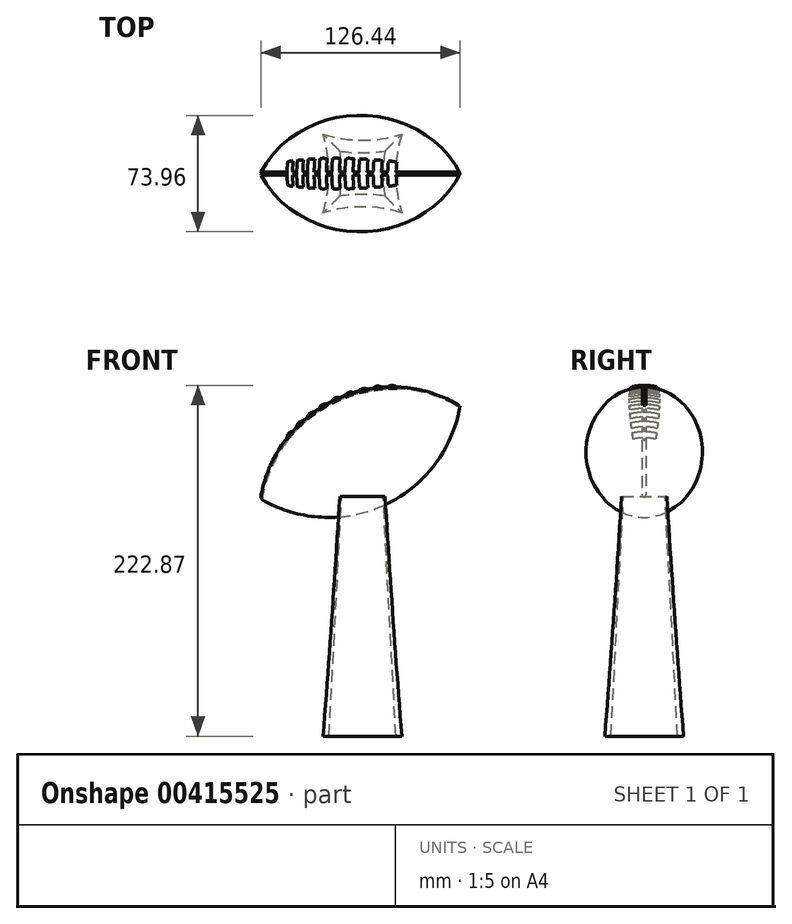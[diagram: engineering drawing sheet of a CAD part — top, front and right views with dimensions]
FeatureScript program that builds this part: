
annotation { "Feature Type Name" : "Feature", "Feature Type Description" : "" }
export const myFeature = defineFeature(function(context is Context, id is Id, definition is map)
    precondition{}
    {
        {
            var Q0;
            Q0=qCreatedBy(makeId("Top.planeOp"),FACE);
            var sketch = newSketch(context, id + "F0", { "sketchPlane" : qUnion([Q0])});
            skLineSegment(sketch, "E0.bottom", {"start": v(25, -25) * mm, "end": v(-25, -25) * mm, "construction": true});
            skLineSegment(sketch, "E0.top", {"start": v(25, 25) * mm, "end": v(-25, 25) * mm, "construction": true});
            skLineSegment(sketch, "E0.left", {"start": v(25, -25) * mm, "end": v(25, 25) * mm, "construction": true});
            skLineSegment(sketch, "E0.right", {"start": v(-25, -25) * mm, "end": v(-25, 25) * mm, "construction": true});
            skPoint(sketch, "E0.middle", {"position": v(0, 0) * mm});
            skArc(sketch, "E1", {"start": v(-25, -25) * mm, "mid": v(-21.18, 0) * mm, "end": v(-25, 25) * mm});
            skArc(sketch, "E2.1.0", {"start": v(25, -25) * mm, "mid": v(0, -21.18) * mm, "end": v(-25, -25) * mm});
            skArc(sketch, "E2.2.0", {"start": v(25, 25) * mm, "mid": v(21.18, 0) * mm, "end": v(25, -25) * mm});
            skArc(sketch, "E2.3.0", {"start": v(-25, 25) * mm, "mid": v(0, 21.18) * mm, "end": v(25, 25) * mm});
            skSolve(sketch);
        }
        {
            var Q0;
            Q0=makeQuery(id+"F0.imprint","IMPRINT",FACE,{"disambiguationData":[TD([[makeQuery(id+"F0.imprint","IMPRINT",EDGE,{"derivedFrom":sQuery(id+"F0.wireOp",EDGE,"E1")}),-1.0]])]});
            extrude(context, id + "F1", {"entities" : qUnion([Q0]), "depth" : 152.4 * mm, "hasDraft" : true, "draftAngle" : 3 * degree, "draftPullDirection" : true});
        }
        {
            var Q0;
            Q0=qCreatedBy(makeId("Front.planeOp"),FACE);
            var sketch = newSketch(context, id + "F2", { "sketchPlane" : qUnion([Q0])});
            skLineSegment(sketch, "E3", {"start": v(91.8, 223.9) * mm, "end": v(-91.96, 138.2) * mm, "construction": true});
            skLineSegment(sketch, "E4", {"start": v(0, 0) * mm, "end": v(0, 249.61) * mm, "construction": true});
            skArc(sketch, "E5", {"start": v(62, 210) * mm, "mid": v(-17.07, 213.93) * mm, "end": v(-64.88, 150.83) * mm});
            skLineSegment(sketch, "E6", {"start": v(62, 210) * mm, "end": v(-64.88, 150.83) * mm});
            skArc(sketch, "E7.0", {"start": v(64.55, 214.3) * mm, "mid": v(-19.18, 218.46) * mm, "end": v(-69.82, 151.64) * mm, "construction": true});
            skLineSegment(sketch, "E8", {"start": v(-17.07, 213.93) * mm, "end": v(-1.44, 180.42) * mm, "construction": true});
            skCircle(sketch, "E9", {"center": v(-15.8, 211.2) * mm, "radius": 4 * mm});
            skCircle(sketch, "E10.1.0", {"center": v(-7.53, 214.53) * mm, "radius": 4 * mm});
            skCircle(sketch, "E10.2.0", {"center": v(1.05, 216.93) * mm, "radius": 4 * mm});
            skCircle(sketch, "E10.3.0", {"center": v(9.85, 218.38) * mm, "radius": 4 * mm});
            skCircle(sketch, "E10.4.0", {"center": v(18.75, 218.87) * mm, "radius": 4 * mm});
            skLineSegment(sketch, "E10.anchor1", {"start": v(18.75, 137.12) * mm, "end": v(-15.8, 211.2) * mm, "construction": true});
            skLineSegment(sketch, "E10.anchor2", {"start": v(18.75, 137.12) * mm, "end": v(18.75, 218.87) * mm, "construction": true});
            skCircle(sketch, "E11.MirrorC", {"center": v(-23.66, 207) * mm, "radius": 4 * mm});
            skCircle(sketch, "E12.MirrorC", {"center": v(-31.02, 201.98) * mm, "radius": 4 * mm});
            skCircle(sketch, "E13.MirrorC", {"center": v(-37.78, 196.17) * mm, "radius": 4 * mm});
            skCircle(sketch, "E14.MirrorC", {"center": v(-43.87, 189.67) * mm, "radius": 4 * mm});
            skSolve(sketch);
        }
        {
            var Q0;
            {var subQ0=sQuery(id+"F2.wireOp",EDGE,"E6");Q0=makeQuery(id+"F2.imprint","IMPRINT",FACE,{"disambiguationData":[TD([[makeQuery(id+"F2.imprint","IMPRINT",EDGE,{"derivedFrom":subQ0}),-1.0]])]});}
            var Q1;
            {var subQ0=sQuery(id+"F2.wireOp",EDGE,"E10.2.0");var subQ1=sQuery(id+"F2.wireOp",EDGE,"E5");var subQ2=makeQuery(id+"F2.imprint","INTERSECT",VERTEX,{"disambiguationData":[OD(0.0)],"derivedFrom":[subQ1,subQ0]});Q1=makeQuery(id+"F2.imprint","IMPRINT",FACE,{"disambiguationData":[TD([[makeQuery(id+"F2.imprint","IMPRINT",EDGE,{"disambiguationData":[TD([[subQ2,-1.0]])],"derivedFrom":subQ1}),1.0]])]});}
            var Q2;
            {var subQ0=sQuery(id+"F2.wireOp",EDGE,"E10.3.0");var subQ1=sQuery(id+"F2.wireOp",EDGE,"E5");var subQ2=makeQuery(id+"F2.imprint","INTERSECT",VERTEX,{"disambiguationData":[OD(0.0)],"derivedFrom":[subQ1,subQ0]});Q2=makeQuery(id+"F2.imprint","IMPRINT",FACE,{"disambiguationData":[TD([[makeQuery(id+"F2.imprint","IMPRINT",EDGE,{"disambiguationData":[TD([[subQ2,-1.0]])],"derivedFrom":subQ1}),1.0]])]});}
            var Q3;
            {var subQ0=sQuery(id+"F2.wireOp",EDGE,"E10.4.0");var subQ1=sQuery(id+"F2.wireOp",EDGE,"E5");var subQ2=makeQuery(id+"F2.imprint","INTERSECT",VERTEX,{"disambiguationData":[OD(0.0)],"derivedFrom":[subQ1,subQ0]});Q3=makeQuery(id+"F2.imprint","IMPRINT",FACE,{"disambiguationData":[TD([[makeQuery(id+"F2.imprint","IMPRINT",EDGE,{"disambiguationData":[TD([[subQ2,-1.0]])],"derivedFrom":subQ1}),1.0]])]});}
            var Q4;
            {var subQ0=sQuery(id+"F2.wireOp",EDGE,"E10.1.0");var subQ1=sQuery(id+"F2.wireOp",EDGE,"E5");var subQ2=makeQuery(id+"F2.imprint","INTERSECT",VERTEX,{"disambiguationData":[OD(0.0)],"derivedFrom":[subQ1,subQ0]});Q4=makeQuery(id+"F2.imprint","IMPRINT",FACE,{"disambiguationData":[TD([[makeQuery(id+"F2.imprint","IMPRINT",EDGE,{"disambiguationData":[TD([[subQ2,-1.0]])],"derivedFrom":subQ1}),1.0]])]});}
            var Q5;
            {var subQ0=sQuery(id+"F2.wireOp",EDGE,"E9");var subQ1=sQuery(id+"F2.wireOp",EDGE,"E5");var subQ2=makeQuery(id+"F2.imprint","INTERSECT",VERTEX,{"disambiguationData":[OD(0.0)],"derivedFrom":[subQ1,subQ0]});Q5=makeQuery(id+"F2.imprint","IMPRINT",FACE,{"disambiguationData":[TD([[makeQuery(id+"F2.imprint","IMPRINT",EDGE,{"disambiguationData":[TD([[subQ2,-1.0]])],"derivedFrom":subQ1}),1.0]])]});}
            var Q6;
            {var subQ0=sQuery(id+"F2.wireOp",EDGE,"E12.MirrorC");var subQ1=sQuery(id+"F2.wireOp",EDGE,"E5");var subQ2=makeQuery(id+"F2.imprint","INTERSECT",VERTEX,{"disambiguationData":[OD(0.0)],"derivedFrom":[subQ1,subQ0]});Q6=makeQuery(id+"F2.imprint","IMPRINT",FACE,{"disambiguationData":[TD([[makeQuery(id+"F2.imprint","IMPRINT",EDGE,{"disambiguationData":[TD([[subQ2,-1.0]])],"derivedFrom":subQ1}),1.0]])]});}
            var Q7;
            {var subQ0=sQuery(id+"F2.wireOp",EDGE,"E11.MirrorC");var subQ1=sQuery(id+"F2.wireOp",EDGE,"E5");var subQ2=makeQuery(id+"F2.imprint","INTERSECT",VERTEX,{"disambiguationData":[OD(0.0)],"derivedFrom":[subQ1,subQ0]});Q7=makeQuery(id+"F2.imprint","IMPRINT",FACE,{"disambiguationData":[TD([[makeQuery(id+"F2.imprint","IMPRINT",EDGE,{"disambiguationData":[TD([[subQ2,-1.0]])],"derivedFrom":subQ1}),1.0]])]});}
            var Q8;
            {var subQ0=sQuery(id+"F2.wireOp",EDGE,"E13.MirrorC");var subQ1=sQuery(id+"F2.wireOp",EDGE,"E5");var subQ2=makeQuery(id+"F2.imprint","INTERSECT",VERTEX,{"disambiguationData":[OD(0.0)],"derivedFrom":[subQ1,subQ0]});Q8=makeQuery(id+"F2.imprint","IMPRINT",FACE,{"disambiguationData":[TD([[makeQuery(id+"F2.imprint","IMPRINT",EDGE,{"disambiguationData":[TD([[subQ2,-1.0]])],"derivedFrom":subQ1}),1.0]])]});}
            var Q9;
            {var subQ0=sQuery(id+"F2.wireOp",EDGE,"E14.MirrorC");var subQ1=sQuery(id+"F2.wireOp",EDGE,"E5");var subQ2=makeQuery(id+"F2.imprint","INTERSECT",VERTEX,{"disambiguationData":[OD(0.0)],"derivedFrom":[subQ1,subQ0]});Q9=makeQuery(id+"F2.imprint","IMPRINT",FACE,{"disambiguationData":[TD([[makeQuery(id+"F2.imprint","IMPRINT",EDGE,{"disambiguationData":[TD([[subQ2,-1.0]])],"derivedFrom":subQ1}),1.0]])]});}
            var Q10;
            Q10=sQuery(id+"F2.wireOp",EDGE,"E3");
            revolve(context, id + "F3", {"entities" : qUnion([Q0, Q1, Q2, Q3, Q4, Q5, Q6, Q7, Q8, Q9]), "axis" : qUnion([Q10]), "revolveType" : RevolveType.FULL});
        }
        {
            var Q0;
            Q0=sQuery(id+"F2.wireOp",VERTEX,"E6.end");
            var Q1;
            Q1=sQuery(id+"F2.wireOp",EDGE,"E3");
            cPlane(context, id + "F4", {"entities" : qUnion([Q0, Q1]), "cplaneType" : CPlaneType.LINE_POINT, "offset" : 25 * mm, "width" : 150 * mm, "height" : 150 * mm});
        }
        {
            var Q0;
            Q0=qCreatedBy(id+"F4.planeOp",FACE);
            var sketch = newSketch(context, id + "F5", { "sketchPlane" : qUnion([Q0])});
            skEllipse(sketch, "E15", {"center": v(0, 188.62) * mm, "majorRadius": 26.65 * mm, "minorRadius": 2.72 * mm, "majorAxis": v(0, -1)});
            skSolve(sketch);
        }
        {
            var Q0;
            Q0=makeQuery(id+"F5.imprint","IMPRINT",FACE,{"disambiguationData":[TD([[makeQuery(id+"F5.imprint","IMPRINT",EDGE,{"derivedFrom":sQuery(id+"F5.wireOp",EDGE,"E15")}),1.0]])]});
            var Q1;
            Q1=sQuery(id+"F2.wireOp",EDGE,"E5");
            sweep(context, id + "F6", {"operationType" : NewBodyOperationType.REMOVE, "profiles" : qUnion([Q0]), "path" : qUnion([Q1])});
        }
        {
            var Q0;
            {var subQ0=sQuery(id+"F2.wireOp",EDGE,"E9");var subQ1=sQuery(id+"F2.wireOp",EDGE,"E5");var subQ2=makeQuery(id+"F2.imprint","INTERSECT",VERTEX,{"disambiguationData":[OD(0.0)],"derivedFrom":[subQ1,subQ0]});Q0=makeQuery(id+"F2.imprint","IMPRINT",FACE,{"disambiguationData":[TD([[makeQuery(id+"F2.imprint","IMPRINT",EDGE,{"disambiguationData":[TD([[subQ2,-1.0]])],"derivedFrom":subQ1}),-1.0]])]});}
            var Q1;
            {var subQ0=sQuery(id+"F2.wireOp",EDGE,"E10.1.0");var subQ1=sQuery(id+"F2.wireOp",EDGE,"E5");var subQ2=makeQuery(id+"F2.imprint","INTERSECT",VERTEX,{"disambiguationData":[OD(0.0)],"derivedFrom":[subQ1,subQ0]});Q1=makeQuery(id+"F2.imprint","IMPRINT",FACE,{"disambiguationData":[TD([[makeQuery(id+"F2.imprint","IMPRINT",EDGE,{"disambiguationData":[TD([[subQ2,-1.0]])],"derivedFrom":subQ1}),-1.0]])]});}
            var Q2;
            {var subQ0=sQuery(id+"F2.wireOp",EDGE,"E10.2.0");var subQ1=sQuery(id+"F2.wireOp",EDGE,"E5");var subQ2=makeQuery(id+"F2.imprint","INTERSECT",VERTEX,{"disambiguationData":[OD(0.0)],"derivedFrom":[subQ1,subQ0]});Q2=makeQuery(id+"F2.imprint","IMPRINT",FACE,{"disambiguationData":[TD([[makeQuery(id+"F2.imprint","IMPRINT",EDGE,{"disambiguationData":[TD([[subQ2,-1.0]])],"derivedFrom":subQ1}),-1.0]])]});}
            var Q3;
            {var subQ0=sQuery(id+"F2.wireOp",EDGE,"E10.3.0");var subQ1=sQuery(id+"F2.wireOp",EDGE,"E5");var subQ2=makeQuery(id+"F2.imprint","INTERSECT",VERTEX,{"disambiguationData":[OD(0.0)],"derivedFrom":[subQ1,subQ0]});Q3=makeQuery(id+"F2.imprint","IMPRINT",FACE,{"disambiguationData":[TD([[makeQuery(id+"F2.imprint","IMPRINT",EDGE,{"disambiguationData":[TD([[subQ2,-1.0]])],"derivedFrom":subQ1}),-1.0]])]});}
            var Q4;
            {var subQ0=sQuery(id+"F2.wireOp",EDGE,"E10.4.0");var subQ1=sQuery(id+"F2.wireOp",EDGE,"E5");var subQ2=makeQuery(id+"F2.imprint","INTERSECT",VERTEX,{"disambiguationData":[OD(0.0)],"derivedFrom":[subQ1,subQ0]});Q4=makeQuery(id+"F2.imprint","IMPRINT",FACE,{"disambiguationData":[TD([[makeQuery(id+"F2.imprint","IMPRINT",EDGE,{"disambiguationData":[TD([[subQ2,-1.0]])],"derivedFrom":subQ1}),-1.0]])]});}
            var Q5;
            {var subQ0=sQuery(id+"F2.wireOp",EDGE,"E10.1.0");var subQ1=sQuery(id+"F2.wireOp",EDGE,"E5");var subQ2=makeQuery(id+"F2.imprint","INTERSECT",VERTEX,{"disambiguationData":[OD(0.0)],"derivedFrom":[subQ1,subQ0]});Q5=makeQuery(id+"F2.imprint","IMPRINT",FACE,{"disambiguationData":[TD([[makeQuery(id+"F2.imprint","IMPRINT",EDGE,{"disambiguationData":[TD([[subQ2,-1.0]])],"derivedFrom":subQ1}),1.0]])]});}
            var Q6;
            {var subQ0=sQuery(id+"F2.wireOp",EDGE,"E9");var subQ1=sQuery(id+"F2.wireOp",EDGE,"E5");var subQ2=makeQuery(id+"F2.imprint","INTERSECT",VERTEX,{"disambiguationData":[OD(0.0)],"derivedFrom":[subQ1,subQ0]});Q6=makeQuery(id+"F2.imprint","IMPRINT",FACE,{"disambiguationData":[TD([[makeQuery(id+"F2.imprint","IMPRINT",EDGE,{"disambiguationData":[TD([[subQ2,-1.0]])],"derivedFrom":subQ1}),1.0]])]});}
            var Q7;
            {var subQ0=sQuery(id+"F2.wireOp",EDGE,"E10.2.0");var subQ1=sQuery(id+"F2.wireOp",EDGE,"E5");var subQ2=makeQuery(id+"F2.imprint","INTERSECT",VERTEX,{"disambiguationData":[OD(0.0)],"derivedFrom":[subQ1,subQ0]});Q7=makeQuery(id+"F2.imprint","IMPRINT",FACE,{"disambiguationData":[TD([[makeQuery(id+"F2.imprint","IMPRINT",EDGE,{"disambiguationData":[TD([[subQ2,-1.0]])],"derivedFrom":subQ1}),1.0]])]});}
            var Q8;
            {var subQ0=sQuery(id+"F2.wireOp",EDGE,"E10.3.0");var subQ1=sQuery(id+"F2.wireOp",EDGE,"E5");var subQ2=makeQuery(id+"F2.imprint","INTERSECT",VERTEX,{"disambiguationData":[OD(0.0)],"derivedFrom":[subQ1,subQ0]});Q8=makeQuery(id+"F2.imprint","IMPRINT",FACE,{"disambiguationData":[TD([[makeQuery(id+"F2.imprint","IMPRINT",EDGE,{"disambiguationData":[TD([[subQ2,-1.0]])],"derivedFrom":subQ1}),1.0]])]});}
            var Q9;
            {var subQ0=sQuery(id+"F2.wireOp",EDGE,"E10.4.0");var subQ1=sQuery(id+"F2.wireOp",EDGE,"E5");var subQ2=makeQuery(id+"F2.imprint","INTERSECT",VERTEX,{"disambiguationData":[OD(0.0)],"derivedFrom":[subQ1,subQ0]});Q9=makeQuery(id+"F2.imprint","IMPRINT",FACE,{"disambiguationData":[TD([[makeQuery(id+"F2.imprint","IMPRINT",EDGE,{"disambiguationData":[TD([[subQ2,-1.0]])],"derivedFrom":subQ1}),1.0]])]});}
            var Q10;
            {var subQ0=sQuery(id+"F2.wireOp",EDGE,"E13.MirrorC");var subQ1=sQuery(id+"F2.wireOp",EDGE,"E5");var subQ2=makeQuery(id+"F2.imprint","INTERSECT",VERTEX,{"disambiguationData":[OD(0.0)],"derivedFrom":[subQ1,subQ0]});Q10=makeQuery(id+"F2.imprint","IMPRINT",FACE,{"disambiguationData":[TD([[makeQuery(id+"F2.imprint","IMPRINT",EDGE,{"disambiguationData":[TD([[subQ2,-1.0]])],"derivedFrom":subQ1}),-1.0]])]});}
            var Q11;
            {var subQ0=sQuery(id+"F2.wireOp",EDGE,"E14.MirrorC");var subQ1=sQuery(id+"F2.wireOp",EDGE,"E5");var subQ2=makeQuery(id+"F2.imprint","INTERSECT",VERTEX,{"disambiguationData":[OD(0.0)],"derivedFrom":[subQ1,subQ0]});Q11=makeQuery(id+"F2.imprint","IMPRINT",FACE,{"disambiguationData":[TD([[makeQuery(id+"F2.imprint","IMPRINT",EDGE,{"disambiguationData":[TD([[subQ2,-1.0]])],"derivedFrom":subQ1}),-1.0]])]});}
            var Q12;
            {var subQ0=sQuery(id+"F2.wireOp",EDGE,"E14.MirrorC");var subQ1=sQuery(id+"F2.wireOp",EDGE,"E5");var subQ2=makeQuery(id+"F2.imprint","INTERSECT",VERTEX,{"disambiguationData":[OD(0.0)],"derivedFrom":[subQ1,subQ0]});Q12=makeQuery(id+"F2.imprint","IMPRINT",FACE,{"disambiguationData":[TD([[makeQuery(id+"F2.imprint","IMPRINT",EDGE,{"disambiguationData":[TD([[subQ2,-1.0]])],"derivedFrom":subQ1}),1.0]])]});}
            var Q13;
            {var subQ0=sQuery(id+"F2.wireOp",EDGE,"E11.MirrorC");var subQ1=sQuery(id+"F2.wireOp",EDGE,"E5");var subQ2=makeQuery(id+"F2.imprint","INTERSECT",VERTEX,{"disambiguationData":[OD(0.0)],"derivedFrom":[subQ1,subQ0]});Q13=makeQuery(id+"F2.imprint","IMPRINT",FACE,{"disambiguationData":[TD([[makeQuery(id+"F2.imprint","IMPRINT",EDGE,{"disambiguationData":[TD([[subQ2,-1.0]])],"derivedFrom":subQ1}),1.0]])]});}
            var Q14;
            {var subQ0=sQuery(id+"F2.wireOp",EDGE,"E13.MirrorC");var subQ1=sQuery(id+"F2.wireOp",EDGE,"E5");var subQ2=makeQuery(id+"F2.imprint","INTERSECT",VERTEX,{"disambiguationData":[OD(0.0)],"derivedFrom":[subQ1,subQ0]});Q14=makeQuery(id+"F2.imprint","IMPRINT",FACE,{"disambiguationData":[TD([[makeQuery(id+"F2.imprint","IMPRINT",EDGE,{"disambiguationData":[TD([[subQ2,-1.0]])],"derivedFrom":subQ1}),1.0]])]});}
            var Q15;
            {var subQ0=sQuery(id+"F2.wireOp",EDGE,"E11.MirrorC");var subQ1=sQuery(id+"F2.wireOp",EDGE,"E5");var subQ2=makeQuery(id+"F2.imprint","INTERSECT",VERTEX,{"disambiguationData":[OD(0.0)],"derivedFrom":[subQ1,subQ0]});Q15=makeQuery(id+"F2.imprint","IMPRINT",FACE,{"disambiguationData":[TD([[makeQuery(id+"F2.imprint","IMPRINT",EDGE,{"disambiguationData":[TD([[subQ2,-1.0]])],"derivedFrom":subQ1}),-1.0]])]});}
            var Q16;
            {var subQ0=sQuery(id+"F2.wireOp",EDGE,"E12.MirrorC");var subQ1=sQuery(id+"F2.wireOp",EDGE,"E5");var subQ2=makeQuery(id+"F2.imprint","INTERSECT",VERTEX,{"disambiguationData":[OD(0.0)],"derivedFrom":[subQ1,subQ0]});Q16=makeQuery(id+"F2.imprint","IMPRINT",FACE,{"disambiguationData":[TD([[makeQuery(id+"F2.imprint","IMPRINT",EDGE,{"disambiguationData":[TD([[subQ2,-1.0]])],"derivedFrom":subQ1}),1.0]])]});}
            var Q17;
            {var subQ0=sQuery(id+"F2.wireOp",EDGE,"E12.MirrorC");var subQ1=sQuery(id+"F2.wireOp",EDGE,"E5");var subQ2=makeQuery(id+"F2.imprint","INTERSECT",VERTEX,{"disambiguationData":[OD(0.0)],"derivedFrom":[subQ1,subQ0]});Q17=makeQuery(id+"F2.imprint","IMPRINT",FACE,{"disambiguationData":[TD([[makeQuery(id+"F2.imprint","IMPRINT",EDGE,{"disambiguationData":[TD([[subQ2,-1.0]])],"derivedFrom":subQ1}),-1.0]])]});}
            var Q18;
            Q18=sQuery(id+"F2.wireOp",EDGE,"E3");
            revolve(context, id + "F7", {"operationType" : NewBodyOperationType.ADD, "entities" : qUnion([Q0, Q1, Q2, Q3, Q4, Q5, Q6, Q7, Q8, Q9, Q10, Q11, Q12, Q13, Q14, Q15, Q16, Q17]), "axis" : qUnion([Q18]), "revolveType" : RevolveType.SYMMETRIC, "angle" : 30 * degree});
        }
    });
